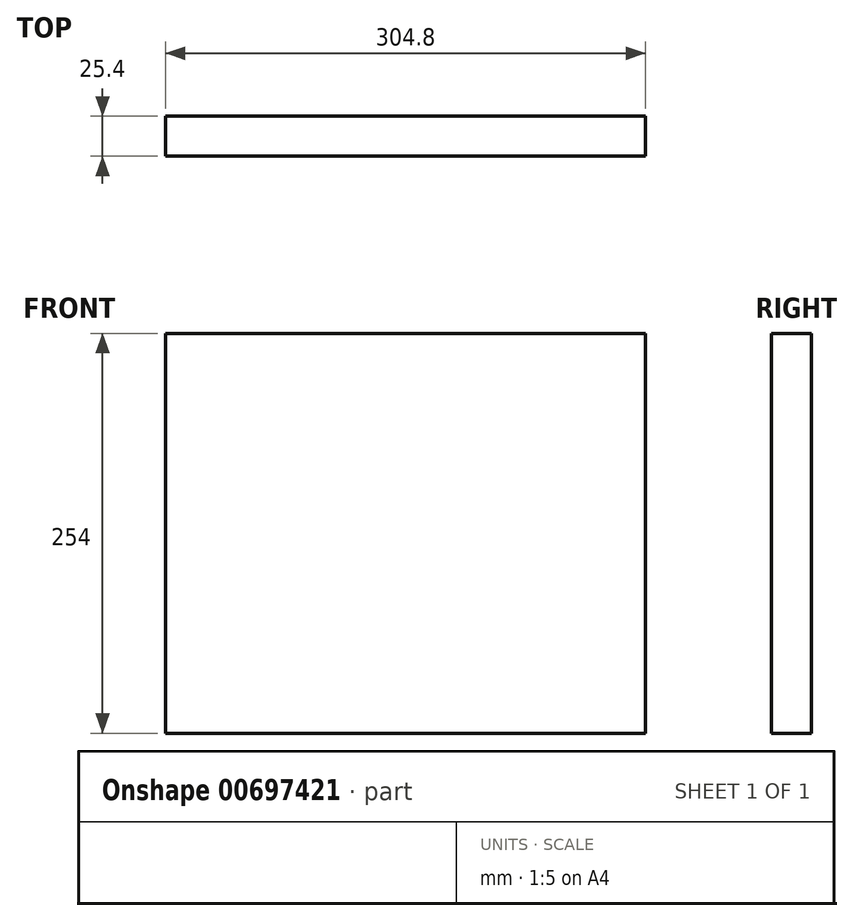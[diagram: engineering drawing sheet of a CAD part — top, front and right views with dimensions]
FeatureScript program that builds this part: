
annotation { "Feature Type Name" : "Feature", "Feature Type Description" : "" }
export const myFeature = defineFeature(function(context is Context, id is Id, definition is map)
    precondition{}
    {
        {
            var Q0;
            Q0=qCreatedBy(makeId("Front.planeOp"),FACE);
            var sketch = newSketch(context, id + "F0", { "sketchPlane" : qUnion([Q0])});
            skLineSegment(sketch, "E0.bottom", {"start": v(-152.4, 127) * mm, "end": v(152.4, 127) * mm});
            skLineSegment(sketch, "E0.top", {"start": v(-152.4, -127) * mm, "end": v(152.4, -127) * mm});
            skLineSegment(sketch, "E0.left", {"start": v(-152.4, 127) * mm, "end": v(-152.4, -127) * mm});
            skLineSegment(sketch, "E0.right", {"start": v(152.4, 127) * mm, "end": v(152.4, -127) * mm});
            skPoint(sketch, "E0.middle", {"position": v(0, 0) * mm});
            skSolve(sketch);
        }
        {
            var Q0;
            Q0 = qSketchRegion(id + "F0", true);
            extrude(context, id + "F1", {"entities" : qUnion([Q0]), "depth" : 25.4 * mm, "offsetDistance" : 25.4 * mm});
        }
    });
